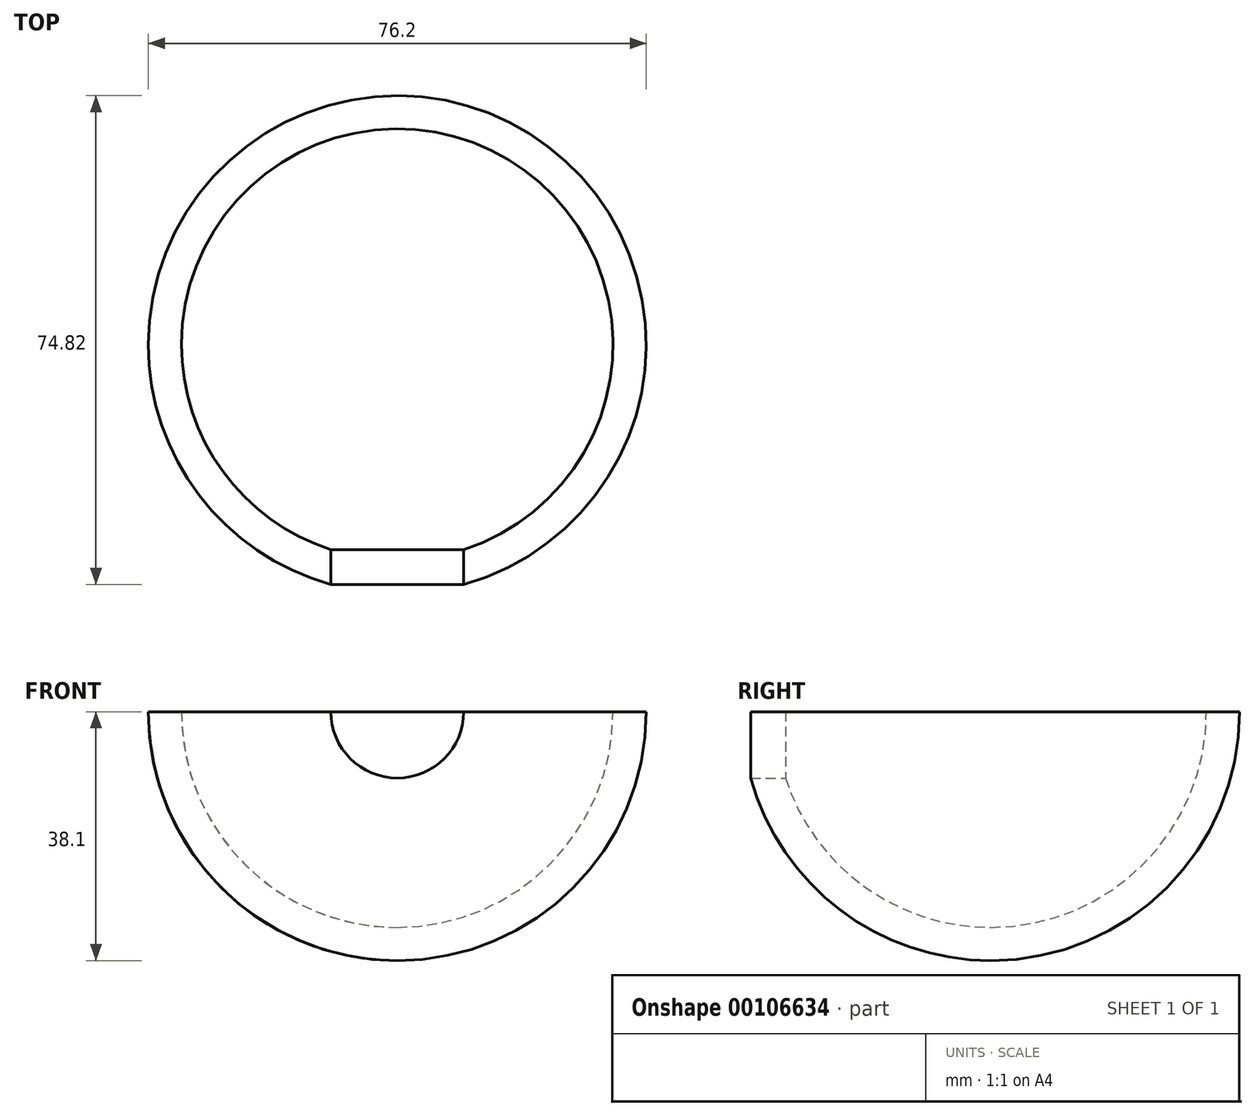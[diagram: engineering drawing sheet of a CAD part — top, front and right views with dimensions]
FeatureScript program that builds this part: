
annotation { "Feature Type Name" : "Feature", "Feature Type Description" : "" }
export const myFeature = defineFeature(function(context is Context, id is Id, definition is map)
    precondition{}
    {
        {
            var Q0;
            Q0=qCreatedBy(makeId("Front.planeOp"),FACE);
            var sketch = newSketch(context, id + "F0", { "sketchPlane" : qUnion([Q0])});
            skLineSegment(sketch, "E0", {"start": v(0, 0) * mm, "end": v(0, -38.1) * mm});
            skLineSegment(sketch, "E1", {"start": v(0, 0) * mm, "end": v(38.1, 0) * mm});
            skArc(sketch, "E2", {"start": v(0, -38.1) * mm, "mid": v(26.94, -26.94) * mm, "end": v(38.1, 0) * mm});
            skSolve(sketch);
        }
        {
            var Q0;
            Q0 = qSketchRegion(id + "F0", true);
            var Q1;
            Q1=sQuery(id+"F0.wireOp",EDGE,"E0");
            revolve(context, id + "F1", {"entities" : qUnion([Q0]), "axis" : qUnion([Q1]), "revolveType" : RevolveType.FULL});
        }
        {
            var Q0;
            Q0=qCreatedBy(makeId("Front.planeOp"),FACE);
            var sketch = newSketch(context, id + "F2", { "sketchPlane" : qUnion([Q0])});
            skLineSegment(sketch, "E3", {"start": v(0, 0) * mm, "end": v(0, -33.02) * mm});
            skLineSegment(sketch, "E4", {"start": v(0, 0) * mm, "end": v(33.02, 0) * mm});
            skArc(sketch, "E5", {"start": v(0, -33.02) * mm, "mid": v(23.35, -23.35) * mm, "end": v(33.02, 0) * mm});
            skSolve(sketch);
        }
        {
            var Q0;
            Q0 = qSketchRegion(id + "F2", true);
            var Q1;
            Q1=sQuery(id+"F2.wireOp",EDGE,"E3");
            revolve(context, id + "F3", {"operationType" : NewBodyOperationType.REMOVE, "entities" : qUnion([Q0]), "axis" : qUnion([Q1]), "revolveType" : RevolveType.FULL, "oppositeDirection" : true});
        }
        {
            var Q0;
            Q0=qCreatedBy(makeId("Front.planeOp"),FACE);
            var sketch = newSketch(context, id + "F4", { "sketchPlane" : qUnion([Q0])});
            skLineSegment(sketch, "E6", {"start": v(0, 0) * mm, "end": v(10.16, 0) * mm});
            skLineSegment(sketch, "E7", {"start": v(0, 0) * mm, "end": v(-10.16, 0) * mm});
            skPoint(sketch, "E7.endSnap0", {"position": v(5.08, 0) * mm});
            skArc(sketch, "E8", {"start": v(-10.16, 0) * mm, "mid": v(0, -10.16) * mm, "end": v(10.16, 0) * mm});
            skSolve(sketch);
        }
        {
            var Q0;
            Q0 = qSketchRegion(id + "F4", true);
            extrude(context, id + "F5", {"entities" : qUnion([Q0]), "operationType" : NewBodyOperationType.REMOVE, "depth" : 38.1 * mm});
        }
    });
